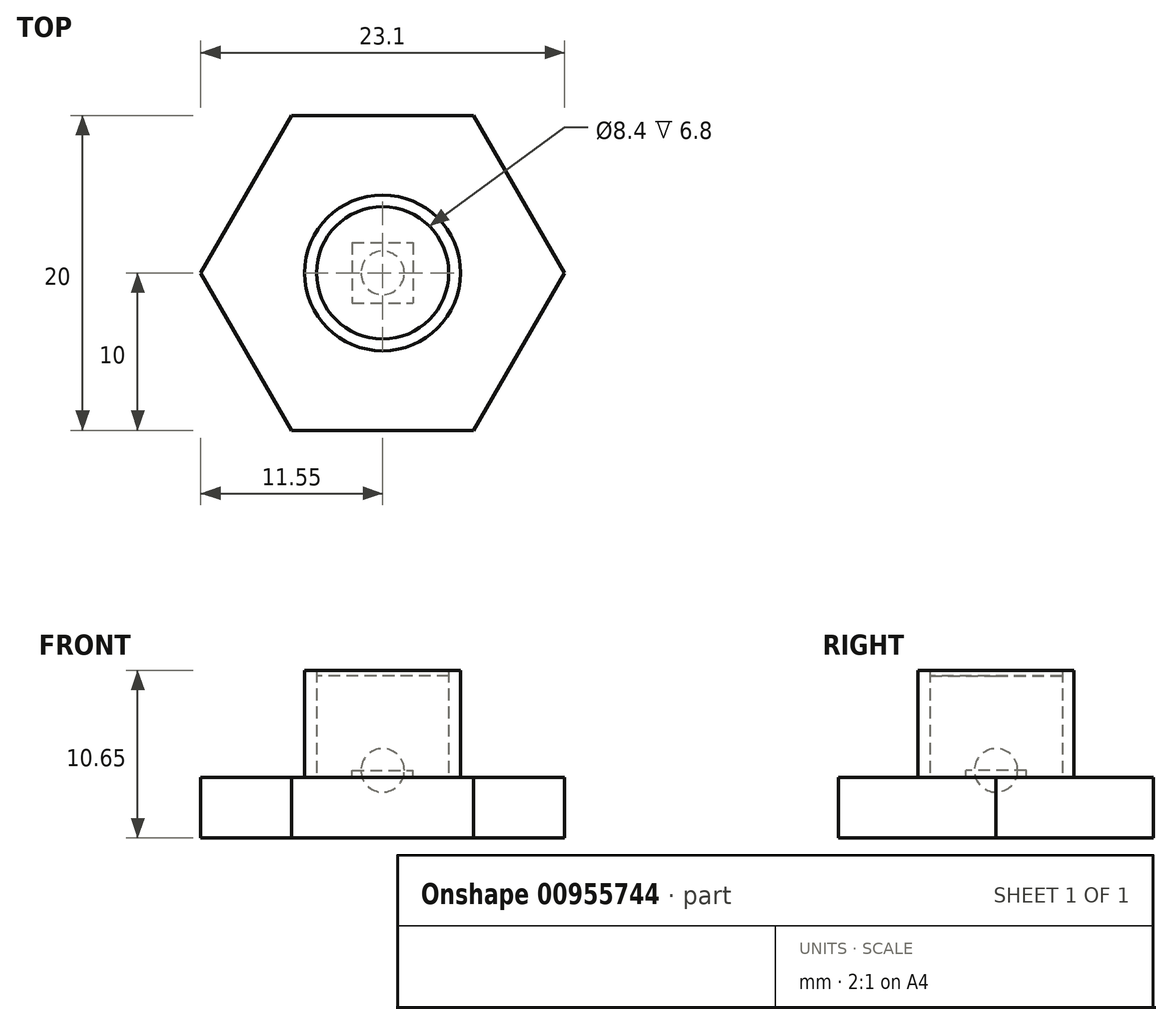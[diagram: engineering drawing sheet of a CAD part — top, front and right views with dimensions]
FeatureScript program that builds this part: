
annotation { "Feature Type Name" : "Feature", "Feature Type Description" : "" }
export const myFeature = defineFeature(function(context is Context, id is Id, definition is map)
    precondition{}
    {
        {
            var Q0;
            Q0=qCreatedBy(makeId("Top.planeOp"),FACE);
            var sketch = newSketch(context, id + "F0", { "sketchPlane" : qUnion([Q0])});
            skCircle(sketch, "E0.cCircle", {"center": v(0, 0) * mm, "radius": 10 * mm, "construction": true});
            skLineSegment(sketch, "E0.0", {"start": v(5.77, -10) * mm, "end": v(-5.77, -10) * mm});
            skLineSegment(sketch, "E0.1", {"start": v(-5.77, -10) * mm, "end": v(-11.55, 0) * mm});
            skLineSegment(sketch, "E0.2", {"start": v(-11.55, 0) * mm, "end": v(-5.77, 10) * mm});
            skLineSegment(sketch, "E0.3", {"start": v(-5.77, 10) * mm, "end": v(5.77, 10) * mm});
            skLineSegment(sketch, "E0.4", {"start": v(5.77, 10) * mm, "end": v(11.55, 0) * mm});
            skLineSegment(sketch, "E0.5", {"start": v(11.55, 0) * mm, "end": v(5.77, -10) * mm});
            skPoint(sketch, "E0.0.midPoint", {"position": v(0, -10) * mm});
            skSolve(sketch);
        }
        {
            var Q0;
            Q0=makeQuery(id+"F0.imprint","IMPRINT",FACE,{"disambiguationData":[TD([[makeQuery(id+"F0.imprint","IMPRINT",EDGE,{"derivedFrom":sQuery(id+"F0.wireOp",EDGE,"E0.0")}),-1.0]])]});
            extrude(context, id + "F1", {"entities" : qUnion([Q0]), "oppositeDirection" : true, "depth" : 4.3 * mm, "offsetDistance" : 25 * mm, "hasSecondDirection" : true, "secondDirectionOppositeDirection" : true, "secondDirectionDepth" : 0.45 * mm});
        }
        {
            var Q0;
            Q0=qCreatedBy(makeId("Top.planeOp"),FACE);
            var sketch = newSketch(context, id + "F2", { "sketchPlane" : qUnion([Q0])});
            skCircle(sketch, "E1", {"center": v(0, 0) * mm, "radius": 1.38 * mm});
            skLineSegment(sketch, "E2", {"start": v(-1.38, 0) * mm, "end": v(1.38, 0) * mm});
            skLineSegment(sketch, "E3.bottom", {"start": v(-1.92, 1.92) * mm, "end": v(1.93, 1.92) * mm});
            skLineSegment(sketch, "E3.top", {"start": v(-1.93, -1.93) * mm, "end": v(1.93, -1.93) * mm});
            skLineSegment(sketch, "E3.left", {"start": v(-1.93, 1.92) * mm, "end": v(-1.92, -1.93) * mm});
            skLineSegment(sketch, "E3.right", {"start": v(1.92, 1.92) * mm, "end": v(1.93, -1.92) * mm});
            skPoint(sketch, "E4", {"position": v(0, 1.92) * mm});
            skPoint(sketch, "E5", {"position": v(1.93, 0) * mm});
            skSolve(sketch);
        }
        {
            var Q0;
            {var subQ0=sQuery(id+"F2.wireOp",EDGE,"E2");Q0=makeQuery(id+"F2.imprint","IMPRINT",FACE,{"disambiguationData":[TD([[makeQuery(id+"F2.imprint","IMPRINT",EDGE,{"derivedFrom":subQ0}),1.0]])]});}
            var Q1;
            Q1=sQuery(id+"F2.wireOp",EDGE,"E1");
            var Q2;
            Q2=sQuery(id+"F2.wireOp",EDGE,"E2");
            revolve(context, id + "F3", {"surfaceOperationType" : NewSurfaceOperationType.NEW, "entities" : qUnion([Q0]), "surfaceEntities" : qUnion([Q1]), "axis" : qUnion([Q2]), "revolveType" : RevolveType.FULL});
        }
        {
            var Q0;
            Q0=makeQuery(id+"F2.imprint","IMPRINT",FACE,{"disambiguationData":[TD([[makeQuery(id+"F2.imprint","IMPRINT",EDGE,{"derivedFrom":sQuery(id+"F2.wireOp",EDGE,"E3.bottom")}),-1.0]])]});
            var Q1;
            {var subQ0=sQuery(id+"F2.wireOp",EDGE,"E2");Q1=makeQuery(id+"F2.imprint","IMPRINT",FACE,{"disambiguationData":[TD([[makeQuery(id+"F2.imprint","IMPRINT",EDGE,{"derivedFrom":subQ0}),1.0]])]});}
            var Q2;
            {var subQ0=sQuery(id+"F2.wireOp",EDGE,"E2");Q2=makeQuery(id+"F2.imprint","IMPRINT",FACE,{"disambiguationData":[TD([[makeQuery(id+"F2.imprint","IMPRINT",EDGE,{"derivedFrom":subQ0}),-1.0]])]});}
            extrude(context, id + "F4", {"entities" : qUnion([Q0, Q1, Q2]), "oppositeDirection" : true, "depth" : 0.45 * mm, "offsetDistance" : 25 * mm});
        }
        {
            var Q0;
            Q0=qCreatedBy(makeId("Top.planeOp"),FACE);
            var sketch = newSketch(context, id + "F5", { "sketchPlane" : qUnion([Q0])});
            skCircle(sketch, "E6", {"center": v(0, 0) * mm, "radius": 4.95 * mm});
            skCircle(sketch, "E7", {"center": v(0, 0) * mm, "radius": 4.2 * mm});
            skSolve(sketch);
        }
        {
            var Q0;
            Q0=makeQuery(id+"F5.imprint","IMPRINT",FACE,{"disambiguationData":[TD([[makeQuery(id+"F5.imprint","IMPRINT",EDGE,{"derivedFrom":sQuery(id+"F5.wireOp",EDGE,"E6")}),1.0]])]});
            extrude(context, id + "F6", {"entities" : qUnion([Q0]), "depth" : 6.35 * mm, "offsetDistance" : 25 * mm, "hasSecondDirection" : true, "secondDirectionOppositeDirection" : true, "secondDirectionDepth" : 0.45 * mm});
        }
        {
            var Q0;
            Q0=makeQuery(id+"F5.imprint","IMPRINT",FACE,{"disambiguationData":[TD([[makeQuery(id+"F5.imprint","IMPRINT",EDGE,{"derivedFrom":sQuery(id+"F5.wireOp",EDGE,"E7")}),1.0]])]});
            extrude(context, id + "F7", {"entities" : qUnion([Q0]), "depth" : 6.35 * mm, "offsetDistance" : 25 * mm, "hasSecondDirection" : true, "secondDirectionOppositeDirection" : false, "secondDirectionDepth" : 6 * mm});
        }
    });
